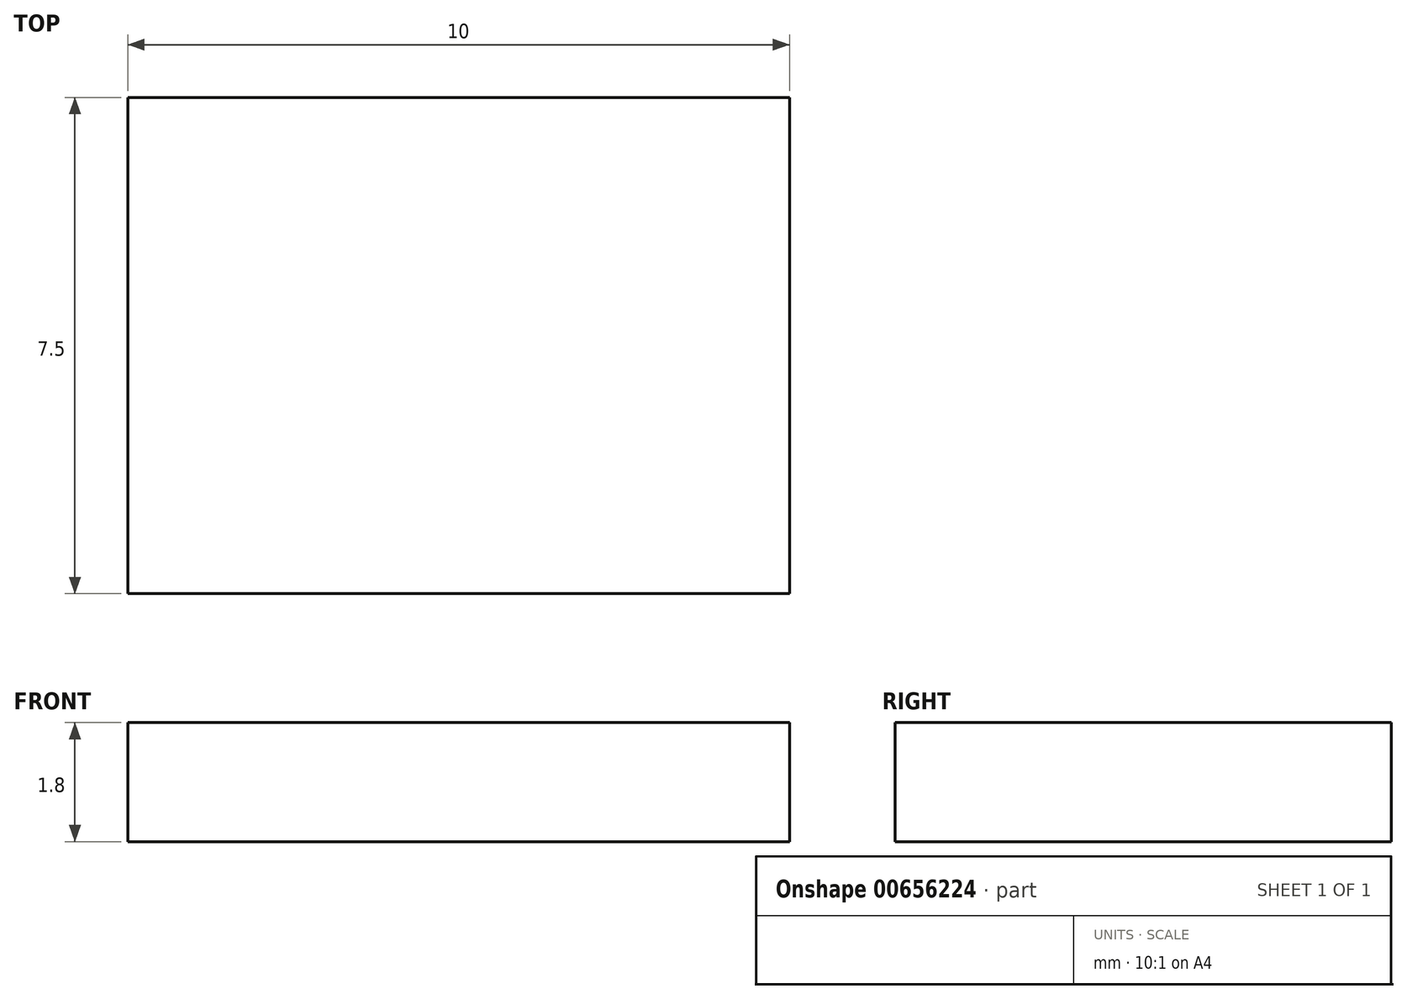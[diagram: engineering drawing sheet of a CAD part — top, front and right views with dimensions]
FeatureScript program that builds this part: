
annotation { "Feature Type Name" : "Feature", "Feature Type Description" : "" }
export const myFeature = defineFeature(function(context is Context, id is Id, definition is map)
    precondition{}
    {
        {
            var Q0;
            Q0=qCreatedBy(makeId("Top.planeOp"),FACE);
            var sketch = newSketch(context, id + "F0", { "sketchPlane" : qUnion([Q0])});
            skLineSegment(sketch, "E0.bottom", {"start": v(-0.07, 5.98) * mm, "end": v(9.93, 5.98) * mm});
            skLineSegment(sketch, "E0.top", {"start": v(-0.07, -1.52) * mm, "end": v(9.93, -1.52) * mm});
            skLineSegment(sketch, "E0.left", {"start": v(-0.07, 5.98) * mm, "end": v(-0.07, -1.52) * mm});
            skLineSegment(sketch, "E0.right", {"start": v(9.93, 5.98) * mm, "end": v(9.93, -1.52) * mm});
            skSolve(sketch);
        }
        {
            var Q0;
            Q0=makeQuery(id+"F0.imprint","IMPRINT",FACE,{"disambiguationData":[TD([[makeQuery(id+"F0.imprint","IMPRINT",EDGE,{"derivedFrom":sQuery(id+"F0.wireOp",EDGE,"E0.bottom")}),-1.0]])]});
            extrude(context, id + "F1", {"entities" : qUnion([Q0]), "depth" : 1.8 * mm, "offsetDistance" : 25 * mm});
        }
    });
